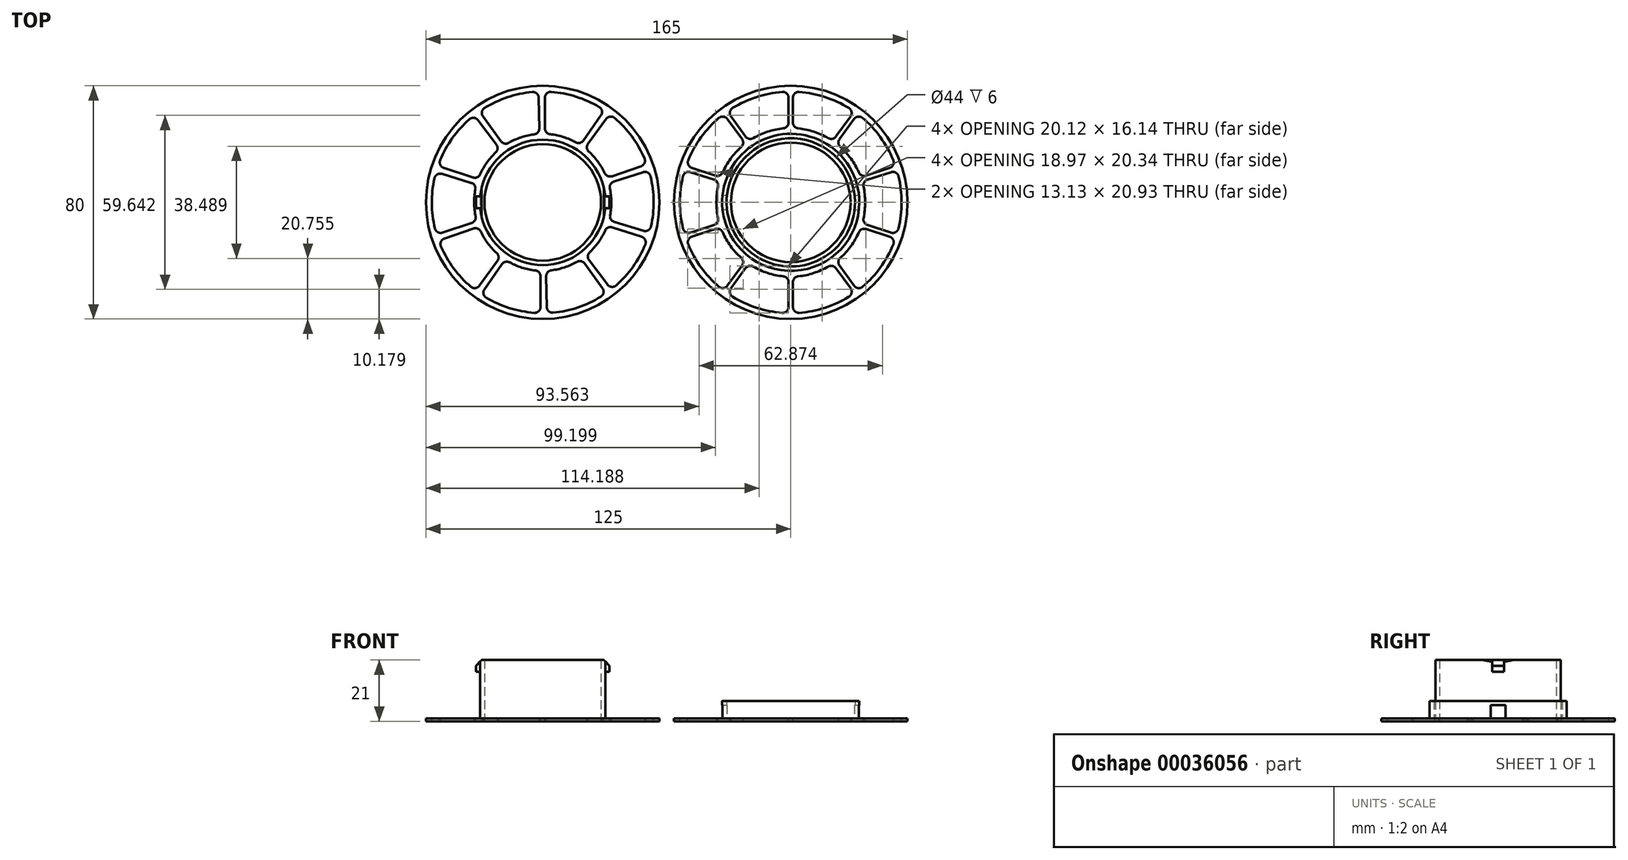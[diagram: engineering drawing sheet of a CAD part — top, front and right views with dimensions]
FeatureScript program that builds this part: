
annotation { "Feature Type Name" : "Feature", "Feature Type Description" : "" }
export const myFeature = defineFeature(function(context is Context, id is Id, definition is map)
    precondition{}
    {
        {
            var Q0;
            Q0=qCreatedBy(makeId("Top.planeOp"),FACE);
            var sketch = newSketch(context, id + "F0", { "sketchPlane" : qUnion([Q0])});
            skCircle(sketch, "E0", {"center": v(0, 0) * mm, "radius": 40 * mm});
            skCircle(sketch, "E1", {"center": v(0, 0) * mm, "radius": 20 * mm});
            skSolve(sketch);
        }
        {
            var Q0;
            Q0 = qSketchRegion(id + "F0", true);
            extrude(context, id + "F1", {"entities" : qUnion([Q0]), "depth" : 1 * mm});
        }
        {
            var Q0;
            Q0=makeQuery(id+"F1.opExtrude","CAP_FACE",FACE,{"disambiguationData":[OSD([sQuery(id+"F0.wireOp",EDGE,"E0"),sQuery(id+"F0.wireOp",EDGE,"E1")])],"isStart":false});
            var sketch = newSketch(context, id + "F2", { "sketchPlane" : qUnion([Q0])});
            skCircle(sketch, "E2", {"center": v(0, 0) * mm, "radius": 21.5 * mm});
            skCircle(sketch, "E3.0", {"center": v(0, 0) * mm, "radius": 20 * mm});
            skSolve(sketch);
        }
        {
            var Q0;
            Q0 = qSketchRegion(id + "F2", true);
            extrude(context, id + "F3", {"entities" : qUnion([Q0]), "operationType" : NewBodyOperationType.ADD, "depth" : 20 * mm});
        }
        {
            var Q0;
            Q0=makeQuery(id+"F3.opExtrude","CAP_FACE",FACE,{"disambiguationData":[OSD([sQuery(id+"F2.wireOp",EDGE,"E2"),sQuery(id+"F2.wireOp",EDGE,"E3.0")])],"isStart":false});
            var sketch = newSketch(context, id + "F4", { "sketchPlane" : qUnion([Q0])});
            skLineSegment(sketch, "E4.bottom", {"start": v(-21.4, 2) * mm, "end": v(-22.9, 2) * mm});
            skLineSegment(sketch, "E4.top", {"start": v(-21.4, -2) * mm, "end": v(-22.9, -2) * mm});
            skLineSegment(sketch, "E4.left", {"start": v(-21.4, 2) * mm, "end": v(-21.4, -2) * mm});
            skLineSegment(sketch, "E4.right", {"start": v(-22.9, 2) * mm, "end": v(-22.9, -2) * mm});
            skLineSegment(sketch, "E5.bottom", {"start": v(21.4, 2) * mm, "end": v(22.9, 2) * mm});
            skLineSegment(sketch, "E5.top", {"start": v(21.4, -2) * mm, "end": v(22.9, -2) * mm});
            skLineSegment(sketch, "E5.left", {"start": v(21.4, 2) * mm, "end": v(21.4, -2) * mm});
            skLineSegment(sketch, "E5.right", {"start": v(22.9, 2) * mm, "end": v(22.9, -2) * mm});
            skLineSegment(sketch, "E6", {"start": v(-21.4, 0) * mm, "end": v(21.4, 0) * mm, "construction": true});
            skSolve(sketch);
        }
        {
            var Q0;
            Q0 = qSketchRegion(id + "F4", true);
            extrude(context, id + "F5", {"entities" : qUnion([Q0]), "operationType" : NewBodyOperationType.ADD, "oppositeDirection" : true, "depth" : 4 * mm});
        }
        {
            var Q0;
            Q0=makeQuery(id+"F5.opExtrude","CAP_EDGE",EDGE,{"disambiguationData":[OSD([sQuery(id+"F4.wireOp",EDGE,"E4.right")])],"isStart":true});
            var Q1;
            Q1=makeQuery(id+"F5.opExtrude","CAP_EDGE",EDGE,{"disambiguationData":[OSD([sQuery(id+"F4.wireOp",EDGE,"E5.right")])],"isStart":true});
            chamfer(context, id + "F6", {"entities" : qUnion([Q0, Q1]), "width" : 2 * mm, "tangentPropagation" : true});
        }
        {
            var Q0;
            Q0=qCreatedBy(makeId("Top.planeOp"),FACE);
            var sketch = newSketch(context, id + "F7", { "sketchPlane" : qUnion([Q0])});
            skCircle(sketch, "E7", {"center": v(85, 0) * mm, "radius": 40 * mm});
            skCircle(sketch, "E8", {"center": v(85, 0) * mm, "radius": 21.5 * mm, "construction": true});
            skCircle(sketch, "E9", {"center": v(85, 0) * mm, "radius": 22 * mm});
            skSolve(sketch);
        }
        {
            var Q0;
            Q0 = qSketchRegion(id + "F7", true);
            extrude(context, id + "F8", {"entities" : qUnion([Q0]), "depth" : 1 * mm});
        }
        {
            var Q0;
            Q0=makeQuery(id+"F8.opExtrude","CAP_FACE",FACE,{"disambiguationData":[OSD([sQuery(id+"F7.wireOp",EDGE,"E7"),sQuery(id+"F7.wireOp",EDGE,"E9")])],"isStart":false});
            var sketch = newSketch(context, id + "F9", { "sketchPlane" : qUnion([Q0])});
            skCircle(sketch, "E10.0", {"center": v(85, 0) * mm, "radius": 22 * mm});
            skCircle(sketch, "E11", {"center": v(85, 0) * mm, "radius": 23.5 * mm});
            skSolve(sketch);
        }
        {
            var Q0;
            Q0 = qSketchRegion(id + "F9", true);
            extrude(context, id + "F10", {"entities" : qUnion([Q0]), "operationType" : NewBodyOperationType.ADD, "depth" : 6 * mm});
        }
        {
            var Q0;
            Q0=makeQuery(id+"F8.opExtrude","CAP_FACE",FACE,{"disambiguationData":[OSD([sQuery(id+"F7.wireOp",EDGE,"E7"),sQuery(id+"F7.wireOp",EDGE,"E9")])],"isStart":false});
            var sketch = newSketch(context, id + "F11", { "sketchPlane" : qUnion([Q0])});
            skLineSegment(sketch, "E12.rect.bottom", {"start": v(61.5, -2.5) * mm, "end": v(108.5, -2.5) * mm});
            skLineSegment(sketch, "E12.rect.top", {"start": v(61.5, 2.5) * mm, "end": v(108.5, 2.5) * mm});
            skLineSegment(sketch, "E12.rect.left", {"start": v(61.5, -2.5) * mm, "end": v(61.5, 2.5) * mm});
            skLineSegment(sketch, "E12.rect.right", {"start": v(108.5, -2.5) * mm, "end": v(108.5, 2.5) * mm});
            skPoint(sketch, "E12.rect.middle", {"position": v(85, 0) * mm});
            skSolve(sketch);
        }
        {
            var Q0;
            Q0 = qSketchRegion(id + "F11", true);
            extrude(context, id + "F12", {"entities" : qUnion([Q0]), "operationType" : NewBodyOperationType.REMOVE, "depth" : 4.5 * mm});
        }
        {
            var Q0;
            Q0=makeQuery(id+"F1.opExtrude","CAP_FACE",FACE,{"disambiguationData":[OSD([sQuery(id+"F0.wireOp",EDGE,"E0"),sQuery(id+"F0.wireOp",EDGE,"E1")])],"isStart":false});
            var sketch = newSketch(context, id + "F13", { "sketchPlane" : qUnion([Q0])});
            skLineSegment(sketch, "E13", {"start": v(0, 23.5) * mm, "end": v(0, 38) * mm, "construction": true});
            skLineSegment(sketch, "E14", {"start": v(21.8, 31.13) * mm, "end": v(13.48, 19.25) * mm, "construction": true});
            skArc(sketch, "E15", {"start": v(13.48, 19.25) * mm, "mid": v(13.17, 19.46) * mm, "end": v(12.86, 19.67) * mm, "construction": true});
            skArc(sketch, "E16", {"start": v(21.8, 31.13) * mm, "mid": v(21.49, 31.34) * mm, "end": v(21.18, 31.55) * mm, "construction": true});
            skLineSegment(sketch, "E17", {"start": v(0.75, 38) * mm, "end": v(0.75, 23.49) * mm});
            skLineSegment(sketch, "E18", {"start": v(12.86, 19.67) * mm, "end": v(21.18, 31.55) * mm});
            skArc(sketch, "E19", {"start": v(0.75, 23.49) * mm, "mid": v(0.38, 23.5) * mm, "end": v(0, 23.5) * mm, "construction": true});
            skArc(sketch, "E20", {"start": v(12.86, 19.67) * mm, "mid": v(7.07, 22.41) * mm, "end": v(0.75, 23.49) * mm});
            skArc(sketch, "E21", {"start": v(21.18, 31.55) * mm, "mid": v(11.43, 36.24) * mm, "end": v(0.75, 38) * mm});
            skArc(sketch, "E22", {"start": v(0.75, 38) * mm, "mid": v(0.38, 38) * mm, "end": v(0, 38) * mm, "construction": true});
            skSolve(sketch);
        }
        {
            var Q0;
            Q0 = qSketchRegion(id + "F13", true);
            extrude(context, id + "F14", {"entities" : qUnion([Q0]), "oppositeDirection" : true, "depth" : 5 * mm});
        }
        {
            var Q0;
            Q0=makeQuery(id+"F14.opExtrude","SWEPT_EDGE",EDGE,{"disambiguationData":[OSD([sQuery(id+"F13.wireOp",EDGE,"E18"),sQuery(id+"F13.wireOp",EDGE,"E21")])]});
            var Q1;
            Q1=makeQuery(id+"F14.opExtrude","SWEPT_EDGE",EDGE,{"disambiguationData":[OSD([sQuery(id+"F13.wireOp",EDGE,"E18"),sQuery(id+"F13.wireOp",EDGE,"E20")])]});
            var Q2;
            Q2=makeQuery(id+"F14.opExtrude","SWEPT_EDGE",EDGE,{"disambiguationData":[OSD([sQuery(id+"F13.wireOp",EDGE,"E17"),sQuery(id+"F13.wireOp",EDGE,"E20")])]});
            var Q3;
            Q3=makeQuery(id+"F14.opExtrude","SWEPT_EDGE",EDGE,{"disambiguationData":[OSD([sQuery(id+"F13.wireOp",EDGE,"E17"),sQuery(id+"F13.wireOp",EDGE,"E21")])]});
            fillet(context, id + "F15", {"entities" : qUnion([Q0, Q1, Q2, Q3]), "radius" : 2 * mm, "tangentPropagation" : true, "allowEdgeOverflow" : false});
        }
        {
            var Q0;
            Q0=makeQuery(id+"F14.opExtrude","SWEPT_BODY",BODY,{"disambiguationData":[OSD([sQuery(id+"F13.wireOp",EDGE,"E17"),sQuery(id+"F13.wireOp",EDGE,"E18"),sQuery(id+"F13.wireOp",EDGE,"E20"),sQuery(id+"F13.wireOp",EDGE,"E21")])]});
            var Q1;
            Q1=makeQuery(id+"F3.boolean.opBoolean","MERGE",FACE,{"derivedFrom":[makeQuery(id+"F1.opExtrude","SWEPT_FACE",FACE,{"disambiguationData":[OSD([sQuery(id+"F0.wireOp",EDGE,"E1")])]}),makeQuery(id+"F3.opExtrude","SWEPT_FACE",FACE,{"disambiguationData":[OSD([sQuery(id+"F2.wireOp",EDGE,"E3.0")])]})]});
            circularPattern(context, id + "F16", {"entities" : qUnion([Q0]), "axis" : qUnion([Q1]), "angle" : 36 * degree, "instanceCount" : 10});
        }
        {
            var Q0;
            Q0=makeQuery(id+"F14.opExtrude","SWEPT_BODY",BODY,{"disambiguationData":[OSD([sQuery(id+"F13.wireOp",EDGE,"E17"),sQuery(id+"F13.wireOp",EDGE,"E18"),sQuery(id+"F13.wireOp",EDGE,"E20"),sQuery(id+"F13.wireOp",EDGE,"E21")])]});
            var Q1;
            Q1=makeQuery(id+"F16.opPattern","COPY",BODY,{"derivedFrom":makeQuery(id+"F14.opExtrude","SWEPT_BODY",BODY,{"disambiguationData":[OSD([sQuery(id+"F13.wireOp",EDGE,"E17"),sQuery(id+"F13.wireOp",EDGE,"E18"),sQuery(id+"F13.wireOp",EDGE,"E20"),sQuery(id+"F13.wireOp",EDGE,"E21")])]}),"instanceName":"1"});
            var Q2;
            Q2=makeQuery(id+"F16.opPattern","COPY",BODY,{"derivedFrom":makeQuery(id+"F14.opExtrude","SWEPT_BODY",BODY,{"disambiguationData":[OSD([sQuery(id+"F13.wireOp",EDGE,"E17"),sQuery(id+"F13.wireOp",EDGE,"E18"),sQuery(id+"F13.wireOp",EDGE,"E20"),sQuery(id+"F13.wireOp",EDGE,"E21")])]}),"instanceName":"2"});
            var Q3;
            Q3=makeQuery(id+"F16.opPattern","COPY",BODY,{"derivedFrom":makeQuery(id+"F14.opExtrude","SWEPT_BODY",BODY,{"disambiguationData":[OSD([sQuery(id+"F13.wireOp",EDGE,"E17"),sQuery(id+"F13.wireOp",EDGE,"E18"),sQuery(id+"F13.wireOp",EDGE,"E20"),sQuery(id+"F13.wireOp",EDGE,"E21")])]}),"instanceName":"3"});
            var Q4;
            Q4=makeQuery(id+"F16.opPattern","COPY",BODY,{"derivedFrom":makeQuery(id+"F14.opExtrude","SWEPT_BODY",BODY,{"disambiguationData":[OSD([sQuery(id+"F13.wireOp",EDGE,"E17"),sQuery(id+"F13.wireOp",EDGE,"E18"),sQuery(id+"F13.wireOp",EDGE,"E20"),sQuery(id+"F13.wireOp",EDGE,"E21")])]}),"instanceName":"4"});
            var Q5;
            Q5=makeQuery(id+"F16.opPattern","COPY",BODY,{"derivedFrom":makeQuery(id+"F14.opExtrude","SWEPT_BODY",BODY,{"disambiguationData":[OSD([sQuery(id+"F13.wireOp",EDGE,"E17"),sQuery(id+"F13.wireOp",EDGE,"E18"),sQuery(id+"F13.wireOp",EDGE,"E20"),sQuery(id+"F13.wireOp",EDGE,"E21")])]}),"instanceName":"5"});
            var Q6;
            Q6=makeQuery(id+"F16.opPattern","COPY",BODY,{"derivedFrom":makeQuery(id+"F14.opExtrude","SWEPT_BODY",BODY,{"disambiguationData":[OSD([sQuery(id+"F13.wireOp",EDGE,"E17"),sQuery(id+"F13.wireOp",EDGE,"E18"),sQuery(id+"F13.wireOp",EDGE,"E20"),sQuery(id+"F13.wireOp",EDGE,"E21")])]}),"instanceName":"6"});
            var Q7;
            Q7=makeQuery(id+"F16.opPattern","COPY",BODY,{"derivedFrom":makeQuery(id+"F14.opExtrude","SWEPT_BODY",BODY,{"disambiguationData":[OSD([sQuery(id+"F13.wireOp",EDGE,"E17"),sQuery(id+"F13.wireOp",EDGE,"E18"),sQuery(id+"F13.wireOp",EDGE,"E20"),sQuery(id+"F13.wireOp",EDGE,"E21")])]}),"instanceName":"8"});
            var Q8;
            Q8=makeQuery(id+"F16.opPattern","COPY",BODY,{"derivedFrom":makeQuery(id+"F14.opExtrude","SWEPT_BODY",BODY,{"disambiguationData":[OSD([sQuery(id+"F13.wireOp",EDGE,"E17"),sQuery(id+"F13.wireOp",EDGE,"E18"),sQuery(id+"F13.wireOp",EDGE,"E20"),sQuery(id+"F13.wireOp",EDGE,"E21")])]}),"instanceName":"9"});
            var Q9;
            Q9=makeQuery(id+"F16.opPattern","COPY",BODY,{"derivedFrom":makeQuery(id+"F14.opExtrude","SWEPT_BODY",BODY,{"disambiguationData":[OSD([sQuery(id+"F13.wireOp",EDGE,"E17"),sQuery(id+"F13.wireOp",EDGE,"E18"),sQuery(id+"F13.wireOp",EDGE,"E20"),sQuery(id+"F13.wireOp",EDGE,"E21")])]}),"instanceName":"7"});
            var Q10;
            Q10=makeQuery(id+"F1.opExtrude","SWEPT_BODY",BODY,{"disambiguationData":[OSD([sQuery(id+"F0.wireOp",EDGE,"E0"),sQuery(id+"F0.wireOp",EDGE,"E1")])]});
            booleanBodies(context, id + "F17", {"operationType" : BooleanOperationType.SUBTRACTION, "tools" : qUnion([Q0, Q1, Q2, Q3, Q4, Q5, Q6, Q7, Q8, Q9]), "targets" : qUnion([Q10])});
        }
        {
            var Q0;
            Q0=makeQuery(id+"F12.boolean.opBoolean","MERGE",FACE,{"derivedFrom":[makeQuery(id+"F8.opExtrude","CAP_FACE",FACE,{"disambiguationData":[OSD([sQuery(id+"F7.wireOp",EDGE,"E7"),sQuery(id+"F7.wireOp",EDGE,"E9")])],"isStart":false}),makeQuery(id+"F12.opExtrude","CAP_FACE",FACE,{"disambiguationData":[OSD([sQuery(id+"F11.wireOp",EDGE,"E12.rect.bottom"),sQuery(id+"F11.wireOp",EDGE,"E12.rect.top"),sQuery(id+"F11.wireOp",EDGE,"E12.rect.left"),sQuery(id+"F11.wireOp",EDGE,"E12.rect.right")])],"isStart":true})]});
            var sketch = newSketch(context, id + "F18", { "sketchPlane" : qUnion([Q0])});
            skLineSegment(sketch, "E23", {"start": v(85, 38) * mm, "end": v(85, 25.5) * mm, "construction": true});
            skLineSegment(sketch, "E24", {"start": v(107.34, 30.74) * mm, "end": v(99.99, 20.63) * mm, "construction": true});
            skArc(sketch, "E25", {"start": v(99.99, 20.63) * mm, "mid": v(99.68, 20.85) * mm, "end": v(99.38, 21.06) * mm, "construction": true});
            skArc(sketch, "E26", {"start": v(107.34, 30.74) * mm, "mid": v(107.03, 30.96) * mm, "end": v(106.72, 31.18) * mm, "construction": true});
            skLineSegment(sketch, "E27", {"start": v(85.75, 38) * mm, "end": v(85.75, 25.49) * mm});
            skLineSegment(sketch, "E28", {"start": v(106.72, 31.18) * mm, "end": v(99.38, 21.06) * mm});
            skArc(sketch, "E29", {"start": v(85.75, 38) * mm, "mid": v(85.38, 38) * mm, "end": v(85, 38) * mm, "construction": true});
            skArc(sketch, "E30", {"start": v(85.75, 25.49) * mm, "mid": v(85.38, 25.5) * mm, "end": v(85, 25.5) * mm, "construction": true});
            skArc(sketch, "E31", {"start": v(99.38, 21.06) * mm, "mid": v(92.88, 24.25) * mm, "end": v(85.75, 25.49) * mm});
            skArc(sketch, "E32", {"start": v(106.72, 31.18) * mm, "mid": v(96.74, 36.14) * mm, "end": v(85.75, 38) * mm});
            skSolve(sketch);
        }
        {
            var Q0;
            Q0 = qSketchRegion(id + "F18", true);
            extrude(context, id + "F19", {"entities" : qUnion([Q0]), "oppositeDirection" : true, "depth" : 5 * mm});
        }
        {
            var Q0;
            Q0=makeQuery(id+"F19.opExtrude","SWEPT_EDGE",EDGE,{"disambiguationData":[OSD([sQuery(id+"F18.wireOp",EDGE,"E27"),sQuery(id+"F18.wireOp",EDGE,"E32")])]});
            var Q1;
            Q1=makeQuery(id+"F19.opExtrude","SWEPT_EDGE",EDGE,{"disambiguationData":[OSD([sQuery(id+"F18.wireOp",EDGE,"E27"),sQuery(id+"F18.wireOp",EDGE,"E31")])]});
            var Q2;
            Q2=makeQuery(id+"F19.opExtrude","SWEPT_EDGE",EDGE,{"disambiguationData":[OSD([sQuery(id+"F18.wireOp",EDGE,"E28"),sQuery(id+"F18.wireOp",EDGE,"E32")])]});
            var Q3;
            Q3=makeQuery(id+"F19.opExtrude","SWEPT_EDGE",EDGE,{"disambiguationData":[OSD([sQuery(id+"F18.wireOp",EDGE,"E28"),sQuery(id+"F18.wireOp",EDGE,"E31")])]});
            fillet(context, id + "F20", {"entities" : qUnion([Q0, Q1, Q2, Q3]), "radius" : 2 * mm, "tangentPropagation" : true, "allowEdgeOverflow" : false});
        }
        {
            var Q0;
            Q0=makeQuery(id+"F19.opExtrude","SWEPT_BODY",BODY,{"disambiguationData":[OSD([sQuery(id+"F18.wireOp",EDGE,"E27"),sQuery(id+"F18.wireOp",EDGE,"E28"),sQuery(id+"F18.wireOp",EDGE,"E31"),sQuery(id+"F18.wireOp",EDGE,"E32")])]});
            var Q1;
            Q1=makeQuery(id+"F10.boolean.opBoolean","MERGE",FACE,{"derivedFrom":[makeQuery(id+"F8.opExtrude","SWEPT_FACE",FACE,{"disambiguationData":[OSD([sQuery(id+"F7.wireOp",EDGE,"E9")])]}),makeQuery(id+"F10.opExtrude","SWEPT_FACE",FACE,{"disambiguationData":[OSD([sQuery(id+"F9.wireOp",EDGE,"E10.0")])]})]});
            circularPattern(context, id + "F21", {"entities" : qUnion([Q0]), "axis" : qUnion([Q1]), "angle" : 36 * degree, "instanceCount" : 10});
        }
        {
            var Q0;
            Q0=makeQuery(id+"F19.opExtrude","SWEPT_BODY",BODY,{"disambiguationData":[OSD([sQuery(id+"F18.wireOp",EDGE,"E27"),sQuery(id+"F18.wireOp",EDGE,"E28"),sQuery(id+"F18.wireOp",EDGE,"E31"),sQuery(id+"F18.wireOp",EDGE,"E32")])]});
            var Q1;
            Q1=makeQuery(id+"F21.opPattern","COPY",BODY,{"derivedFrom":makeQuery(id+"F19.opExtrude","SWEPT_BODY",BODY,{"disambiguationData":[OSD([sQuery(id+"F18.wireOp",EDGE,"E27"),sQuery(id+"F18.wireOp",EDGE,"E28"),sQuery(id+"F18.wireOp",EDGE,"E31"),sQuery(id+"F18.wireOp",EDGE,"E32")])]}),"instanceName":"1"});
            var Q2;
            Q2=makeQuery(id+"F21.opPattern","COPY",BODY,{"derivedFrom":makeQuery(id+"F19.opExtrude","SWEPT_BODY",BODY,{"disambiguationData":[OSD([sQuery(id+"F18.wireOp",EDGE,"E27"),sQuery(id+"F18.wireOp",EDGE,"E28"),sQuery(id+"F18.wireOp",EDGE,"E31"),sQuery(id+"F18.wireOp",EDGE,"E32")])]}),"instanceName":"2"});
            var Q3;
            Q3=makeQuery(id+"F21.opPattern","COPY",BODY,{"derivedFrom":makeQuery(id+"F19.opExtrude","SWEPT_BODY",BODY,{"disambiguationData":[OSD([sQuery(id+"F18.wireOp",EDGE,"E27"),sQuery(id+"F18.wireOp",EDGE,"E28"),sQuery(id+"F18.wireOp",EDGE,"E31"),sQuery(id+"F18.wireOp",EDGE,"E32")])]}),"instanceName":"3"});
            var Q4;
            Q4=makeQuery(id+"F21.opPattern","COPY",BODY,{"derivedFrom":makeQuery(id+"F19.opExtrude","SWEPT_BODY",BODY,{"disambiguationData":[OSD([sQuery(id+"F18.wireOp",EDGE,"E27"),sQuery(id+"F18.wireOp",EDGE,"E28"),sQuery(id+"F18.wireOp",EDGE,"E31"),sQuery(id+"F18.wireOp",EDGE,"E32")])]}),"instanceName":"4"});
            var Q5;
            Q5=makeQuery(id+"F21.opPattern","COPY",BODY,{"derivedFrom":makeQuery(id+"F19.opExtrude","SWEPT_BODY",BODY,{"disambiguationData":[OSD([sQuery(id+"F18.wireOp",EDGE,"E27"),sQuery(id+"F18.wireOp",EDGE,"E28"),sQuery(id+"F18.wireOp",EDGE,"E31"),sQuery(id+"F18.wireOp",EDGE,"E32")])]}),"instanceName":"5"});
            var Q6;
            Q6=makeQuery(id+"F21.opPattern","COPY",BODY,{"derivedFrom":makeQuery(id+"F19.opExtrude","SWEPT_BODY",BODY,{"disambiguationData":[OSD([sQuery(id+"F18.wireOp",EDGE,"E27"),sQuery(id+"F18.wireOp",EDGE,"E28"),sQuery(id+"F18.wireOp",EDGE,"E31"),sQuery(id+"F18.wireOp",EDGE,"E32")])]}),"instanceName":"6"});
            var Q7;
            Q7=makeQuery(id+"F21.opPattern","COPY",BODY,{"derivedFrom":makeQuery(id+"F19.opExtrude","SWEPT_BODY",BODY,{"disambiguationData":[OSD([sQuery(id+"F18.wireOp",EDGE,"E27"),sQuery(id+"F18.wireOp",EDGE,"E28"),sQuery(id+"F18.wireOp",EDGE,"E31"),sQuery(id+"F18.wireOp",EDGE,"E32")])]}),"instanceName":"7"});
            var Q8;
            Q8=makeQuery(id+"F21.opPattern","COPY",BODY,{"derivedFrom":makeQuery(id+"F19.opExtrude","SWEPT_BODY",BODY,{"disambiguationData":[OSD([sQuery(id+"F18.wireOp",EDGE,"E27"),sQuery(id+"F18.wireOp",EDGE,"E28"),sQuery(id+"F18.wireOp",EDGE,"E31"),sQuery(id+"F18.wireOp",EDGE,"E32")])]}),"instanceName":"8"});
            var Q9;
            Q9=makeQuery(id+"F21.opPattern","COPY",BODY,{"derivedFrom":makeQuery(id+"F19.opExtrude","SWEPT_BODY",BODY,{"disambiguationData":[OSD([sQuery(id+"F18.wireOp",EDGE,"E27"),sQuery(id+"F18.wireOp",EDGE,"E28"),sQuery(id+"F18.wireOp",EDGE,"E31"),sQuery(id+"F18.wireOp",EDGE,"E32")])]}),"instanceName":"9"});
            var Q10;
            Q10=makeQuery(id+"F8.opExtrude","SWEPT_BODY",BODY,{"disambiguationData":[OSD([sQuery(id+"F7.wireOp",EDGE,"E7"),sQuery(id+"F7.wireOp",EDGE,"E9")])]});
            booleanBodies(context, id + "F22", {"operationType" : BooleanOperationType.SUBTRACTION, "tools" : qUnion([Q0, Q1, Q2, Q3, Q4, Q5, Q6, Q7, Q8, Q9]), "targets" : qUnion([Q10])});
        }
        {
            var Q0;
            Q0=makeQuery(id+"F8.opExtrude","CAP_FACE",FACE,{"disambiguationData":[OSD([sQuery(id+"F7.wireOp",EDGE,"E7"),sQuery(id+"F7.wireOp",EDGE,"E9")])],"isStart":true});
            var sketch = newSketch(context, id + "F23", { "sketchPlane" : qUnion([Q0])});
            skCircle(sketch, "E33.0", {"center": v(85, 0) * mm, "radius": 22 * mm});
            skCircle(sketch, "E34", {"center": v(85, 0) * mm, "radius": 20.5 * mm});
            skSolve(sketch);
        }
        {
            var Q0;
            Q0 = qSketchRegion(id + "F23", true);
            extrude(context, id + "F24", {"entities" : qUnion([Q0]), "operationType" : NewBodyOperationType.ADD, "oppositeDirection" : true, "depth" : 1 * mm});
        }
    });
